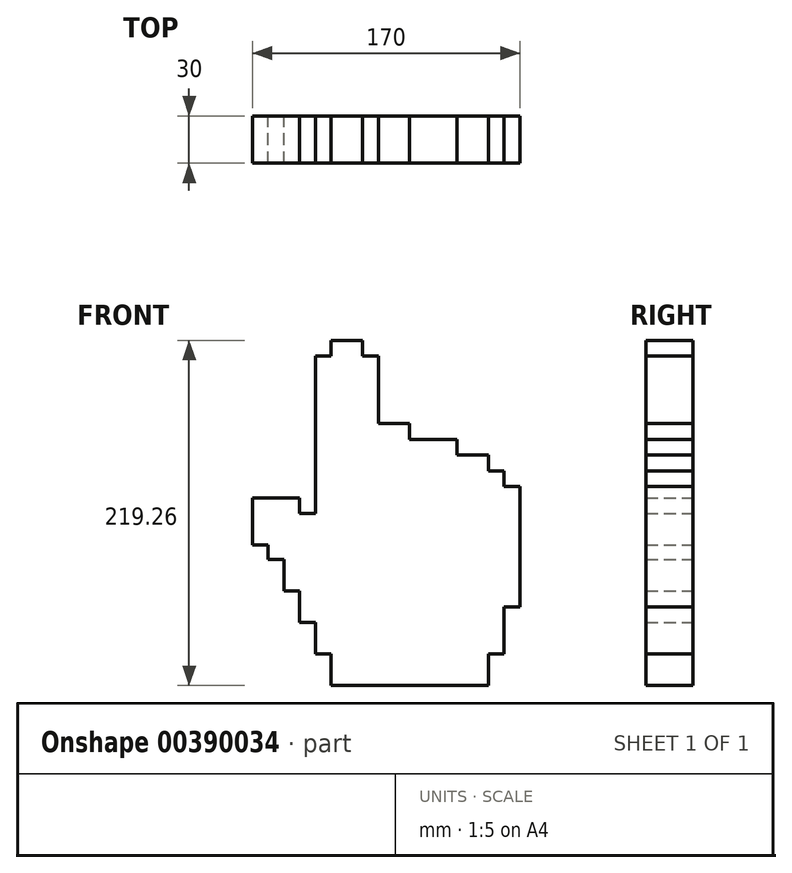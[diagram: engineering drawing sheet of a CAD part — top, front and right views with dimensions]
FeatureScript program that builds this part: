
annotation { "Feature Type Name" : "Feature", "Feature Type Description" : "" }
export const myFeature = defineFeature(function(context is Context, id is Id, definition is map)
    precondition{}
    {
        {
            var Q0;
            Q0=qCreatedBy(makeId("Front.planeOp"),FACE);
            var sketch = newSketch(context, id + "F0", { "sketchPlane" : qUnion([Q0])});
            skLineSegment(sketch, "E0", {"start": v(-31.63, -39) * mm, "end": v(68.37, -39) * mm});
            skLineSegment(sketch, "E1", {"start": v(-31.63, -39) * mm, "end": v(-31.63, -19) * mm});
            skLineSegment(sketch, "E2", {"start": v(-31.63, -19) * mm, "end": v(-41.63, -19) * mm});
            skLineSegment(sketch, "E3", {"start": v(-41.63, -19) * mm, "end": v(-41.63, 1) * mm});
            skLineSegment(sketch, "E4", {"start": v(-41.63, 1) * mm, "end": v(-51.63, 1) * mm});
            skLineSegment(sketch, "E5", {"start": v(-51.63, 1) * mm, "end": v(-51.63, 21) * mm});
            skLineSegment(sketch, "E6", {"start": v(-51.63, 21) * mm, "end": v(-61.63, 21) * mm});
            skLineSegment(sketch, "E7", {"start": v(-61.63, 21) * mm, "end": v(-61.63, 41) * mm});
            skLineSegment(sketch, "E8", {"start": v(-61.63, 41) * mm, "end": v(-71.63, 41) * mm});
            skLineSegment(sketch, "E9", {"start": v(-71.63, 41) * mm, "end": v(-71.63, 50.26) * mm});
            skLineSegment(sketch, "E10", {"start": v(-71.63, 50.26) * mm, "end": v(-81.63, 50.26) * mm});
            skLineSegment(sketch, "E11", {"start": v(-81.63, 50.26) * mm, "end": v(-81.63, 80.26) * mm});
            skLineSegment(sketch, "E12", {"start": v(-81.63, 80.26) * mm, "end": v(-51.63, 80.26) * mm});
            skLineSegment(sketch, "E13", {"start": v(-51.63, 80.26) * mm, "end": v(-51.63, 70.26) * mm});
            skLineSegment(sketch, "E14", {"start": v(-51.63, 70.26) * mm, "end": v(-41.63, 70.26) * mm});
            skLineSegment(sketch, "E15", {"start": v(-41.63, 70.26) * mm, "end": v(-41.63, 170.26) * mm});
            skLineSegment(sketch, "E16", {"start": v(-41.63, 170.26) * mm, "end": v(-31.63, 170.26) * mm});
            skLineSegment(sketch, "E17", {"start": v(-31.63, 170.26) * mm, "end": v(-31.63, 180.26) * mm});
            skLineSegment(sketch, "E18", {"start": v(-31.63, 180.26) * mm, "end": v(-11.63, 180.26) * mm});
            skLineSegment(sketch, "E19", {"start": v(-11.63, 180.26) * mm, "end": v(-11.63, 170.26) * mm});
            skLineSegment(sketch, "E20", {"start": v(-11.63, 170.26) * mm, "end": v(-1.63, 170.26) * mm});
            skLineSegment(sketch, "E21", {"start": v(-1.63, 127.38) * mm, "end": v(18.37, 127.38) * mm});
            skLineSegment(sketch, "E22", {"start": v(18.37, 127.38) * mm, "end": v(18.37, 117.38) * mm});
            skLineSegment(sketch, "E23", {"start": v(18.37, 117.38) * mm, "end": v(48.37, 117.38) * mm});
            skLineSegment(sketch, "E24", {"start": v(48.37, 117.38) * mm, "end": v(48.37, 107.38) * mm});
            skLineSegment(sketch, "E25", {"start": v(48.37, 107.38) * mm, "end": v(68.37, 107.38) * mm});
            skLineSegment(sketch, "E26", {"start": v(68.37, 107.38) * mm, "end": v(68.37, 97.38) * mm});
            skLineSegment(sketch, "E27", {"start": v(68.37, 97.38) * mm, "end": v(78.37, 97.38) * mm});
            skLineSegment(sketch, "E28", {"start": v(78.37, 97.38) * mm, "end": v(78.37, 87.38) * mm});
            skLineSegment(sketch, "E29", {"start": v(78.37, 87.38) * mm, "end": v(88.37, 87.38) * mm});
            skLineSegment(sketch, "E30", {"start": v(88.37, 87.38) * mm, "end": v(88.37, 11) * mm});
            skLineSegment(sketch, "E31", {"start": v(88.37, 11) * mm, "end": v(78.37, 11) * mm});
            skLineSegment(sketch, "E32", {"start": v(78.37, 11) * mm, "end": v(78.37, -19) * mm});
            skLineSegment(sketch, "E33", {"start": v(78.37, -19) * mm, "end": v(68.37, -19) * mm});
            skLineSegment(sketch, "E34", {"start": v(68.37, -19) * mm, "end": v(68.37, -39) * mm});
            skLineSegment(sketch, "E35", {"start": v(-1.63, 170.26) * mm, "end": v(-1.63, 127.38) * mm});
            skSolve(sketch);
        }
        {
            var Q0;
            Q0=makeQuery(id+"F0.imprint","IMPRINT",FACE,{"disambiguationData":[TD([[makeQuery(id+"F0.imprint","IMPRINT",EDGE,{"derivedFrom":sQuery(id+"F0.wireOp",EDGE,"E0")}),1.0]])]});
            extrude(context, id + "F1", {"entities" : qUnion([Q0]), "depth" : 30 * mm});
        }
    });
